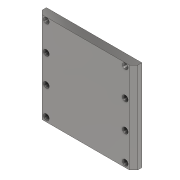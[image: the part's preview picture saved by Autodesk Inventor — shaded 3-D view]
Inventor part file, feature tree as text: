
AUTODESK INVENTOR PART (.ipt)
format: ipt  version: 2020.3 (Build 243373010, 373A)  size: 121,344 bytes
history: native  units: mm
features: extrude x1, chamfer x1, sketch x1
ambient origin geometry x8: Origin, YZ Plane, XZ Plane, XY Plane, X Axis, Y Axis, Z Axis, Center Point
bodies: Solid1 (feature_tree)
feature tree (3):
  extrude  "Extrusion1"  Depth=109.35mm TaperAngle=45.0deg
  chamfer  "Chamfer1"  Distance=115.0mm
  sketch  "Sketch1"  dims[d2=10.0mm d3=0.0mm d4=5.0mm d5=2.0mm d6=45.0deg d8=115.0mm d9=109.35mm d10=3.633mm]
